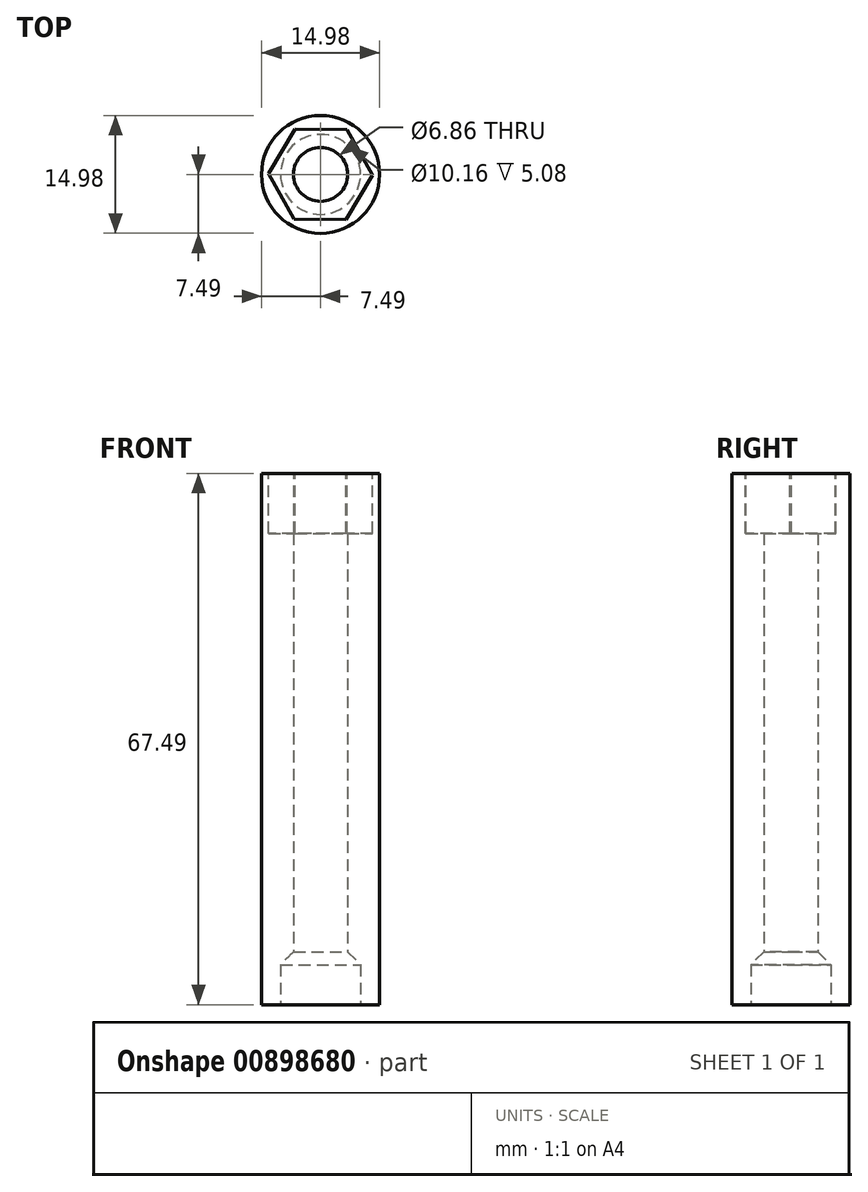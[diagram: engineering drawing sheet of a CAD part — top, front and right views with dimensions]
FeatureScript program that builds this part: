
annotation { "Feature Type Name" : "Feature", "Feature Type Description" : "" }
export const myFeature = defineFeature(function(context is Context, id is Id, definition is map)
    precondition{}
    {
        {
            var Q0;
            Q0=qCreatedBy(makeId("Top.planeOp"),FACE);
            var sketch = newSketch(context, id + "F0", { "sketchPlane" : qUnion([Q0])});
            skCircle(sketch, "E0", {"center": v(0, 0) * mm, "radius": 3.43 * mm});
            skCircle(sketch, "E1", {"center": v(0, 0) * mm, "radius": 5.08 * mm});
            skCircle(sketch, "E2", {"center": v(0, 0) * mm, "radius": 7.5 * mm});
            skSolve(sketch);
        }
        {
            var Q0;
            Q0=qSketchRegion(id+"F0",true);
            var Q1;
            Q1=makeQuery(id+"F0.imprint","IMPRINT",FACE,{"disambiguationData":[TD([[makeQuery(id+"F0.imprint","IMPRINT",EDGE,{"derivedFrom":sQuery(id+"F0.wireOp",EDGE,"E0")}),-1.0]])]});
            extrude(context, id + "F1", {"entities" : qUnion([Q0, Q1]), "depth" : 67.49 * mm, "offsetDistance" : 25.4 * mm});
        }
        {
            var Q0;
            Q0=makeQuery(id+"F1.opExtrude","CAP_FACE",FACE,{"disambiguationData":[OSD([sQuery(id+"F0.wireOp",EDGE,"E0"),sQuery(id+"F0.wireOp",EDGE,"E2")])],"isStart":true});
            var sketch = newSketch(context, id + "F2", { "sketchPlane" : qUnion([Q0])});
            skCircle(sketch, "E3", {"center": v(0, 0) * mm, "radius": 5.08 * mm});
            skSolve(sketch);
        }
        {
            var Q0;
            Q0=makeQuery(id+"F2.imprint","IMPRINT",FACE,{"disambiguationData":[TD([[makeQuery(id+"F2.imprint","IMPRINT",EDGE,{"derivedFrom":makeQuery(id+"F1.opExtrude","CAP_EDGE",EDGE,{"disambiguationData":[OSD([sQuery(id+"F0.wireOp",EDGE,"E0")])],"isStart":true})}),-1.0]])]});
            var Q1;
            Q1=makeQuery(id+"F2.imprint","IMPRINT",FACE,{"disambiguationData":[TD([[makeQuery(id+"F2.imprint","IMPRINT",EDGE,{"derivedFrom":sQuery(id+"F2.wireOp",EDGE,"E3")}),1.0]])]});
            extrude(context, id + "F3", {"entities" : qUnion([Q0, Q1]), "operationType" : NewBodyOperationType.REMOVE, "oppositeDirection" : true, "depth" : 5.08 * mm, "offsetDistance" : 25.4 * mm});
        }
        {
            var Q0;
            Q0=makeQuery(id+"F3.boolean.opBoolean","INTERSECT",EDGE,{"derivedFrom":[makeQuery(id+"F1.opExtrude","SWEPT_FACE",FACE,{"disambiguationData":[OSD([sQuery(id+"F0.wireOp",EDGE,"E0")])]}),makeQuery(id+"F3.opExtrude","CAP_FACE",FACE,{"disambiguationData":[OSD([sQuery(id+"F2.wireOp",EDGE,"E3")])],"isStart":false})]});
            chamfer(context, id + "F4", {"entities" : qUnion([Q0]), "width" : 1.65 * mm, "tangentPropagation" : true});
        }
        {
            var Q0;
            Q0=makeQuery(id+"F1.opExtrude","CAP_FACE",FACE,{"disambiguationData":[OSD([sQuery(id+"F0.wireOp",EDGE,"E0"),sQuery(id+"F0.wireOp",EDGE,"E2")])],"isStart":false});
            var sketch = newSketch(context, id + "F5", { "sketchPlane" : qUnion([Q0])});
            skCircle(sketch, "E4.cCircle", {"center": v(0, 0) * mm, "radius": 6.6 * mm, "construction": true});
            skLineSegment(sketch, "E4.0", {"start": v(3.37, 5.68) * mm, "end": v(6.6, -0.08) * mm});
            skLineSegment(sketch, "E4.1", {"start": v(6.6, -0.08) * mm, "end": v(3.23, -5.76) * mm});
            skLineSegment(sketch, "E4.2", {"start": v(3.23, -5.76) * mm, "end": v(-3.37, -5.68) * mm});
            skLineSegment(sketch, "E4.3", {"start": v(-3.37, -5.68) * mm, "end": v(-6.6, 0.08) * mm});
            skLineSegment(sketch, "E4.4", {"start": v(-6.6, 0.08) * mm, "end": v(-3.23, 5.76) * mm});
            skLineSegment(sketch, "E4.5", {"start": v(-3.23, 5.76) * mm, "end": v(3.37, 5.68) * mm});
            skSolve(sketch);
        }
        {
            var Q0;
            Q0=makeQuery(id+"F5.imprint","IMPRINT",FACE,{"disambiguationData":[TD([[makeQuery(id+"F5.imprint","IMPRINT",EDGE,{"derivedFrom":makeQuery(id+"F1.opExtrude","CAP_EDGE",EDGE,{"disambiguationData":[OSD([sQuery(id+"F0.wireOp",EDGE,"E0")])],"isStart":false})}),1.0]])]});
            var Q1;
            Q1=makeQuery(id+"F5.imprint","IMPRINT",FACE,{"disambiguationData":[TD([[makeQuery(id+"F5.imprint","IMPRINT",EDGE,{"derivedFrom":sQuery(id+"F5.wireOp",EDGE,"E4.0")}),-1.0]])]});
            extrude(context, id + "F6", {"entities" : qUnion([Q0, Q1]), "operationType" : NewBodyOperationType.REMOVE, "oppositeDirection" : true, "depth" : 7.62 * mm, "offsetDistance" : 25.4 * mm});
        }
    });
